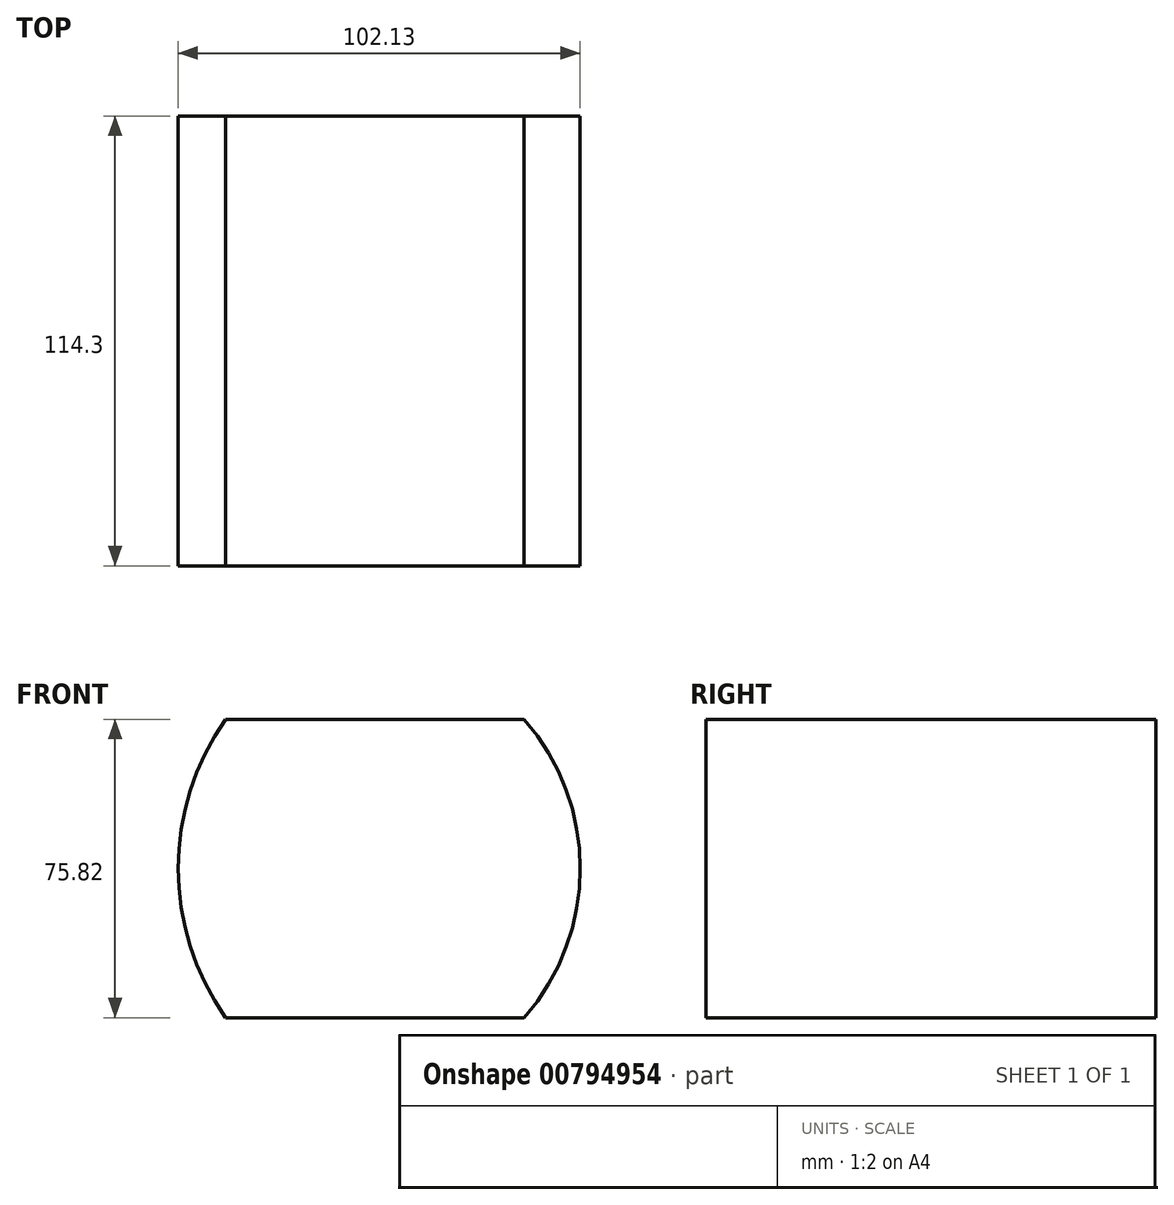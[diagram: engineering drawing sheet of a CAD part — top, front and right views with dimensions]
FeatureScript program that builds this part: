
annotation { "Feature Type Name" : "Feature", "Feature Type Description" : "" }
export const myFeature = defineFeature(function(context is Context, id is Id, definition is map)
    precondition{}
    {
        {
            var Q0;
            Q0=qCreatedBy(makeId("Front.planeOp"),FACE);
            var sketch = newSketch(context, id + "F0", { "sketchPlane" : qUnion([Q0])});
            skLineSegment(sketch, "E0.bottom", {"start": v(37.91, 37.91) * mm, "end": v(-37.91, 37.91) * mm});
            skLineSegment(sketch, "E0.top", {"start": v(37.91, -37.91) * mm, "end": v(-37.91, -37.91) * mm});
            skLineSegment(sketch, "E0.left", {"start": v(37.91, 37.91) * mm, "end": v(37.91, -37.91) * mm});
            skLineSegment(sketch, "E0.right", {"start": v(-37.91, 37.91) * mm, "end": v(-37.91, -37.91) * mm});
            skPoint(sketch, "E0.middle", {"position": v(0, 0) * mm});
            skArc(sketch, "E1", {"start": v(-37.91, 37.91) * mm, "mid": v(-50, 0) * mm, "end": v(-37.91, -37.91) * mm});
            skArc(sketch, "E2", {"start": v(37.91, -37.91) * mm, "mid": v(52.13, 0) * mm, "end": v(37.91, 37.91) * mm});
            skSolve(sketch);
        }
        {
            var Q0;
            Q0 = qSketchRegion(id + "F0", true);
            extrude(context, id + "F1", {"entities" : qUnion([Q0]), "depth" : 114.3 * mm, "offsetDistance" : 25.4 * mm});
        }
    });
